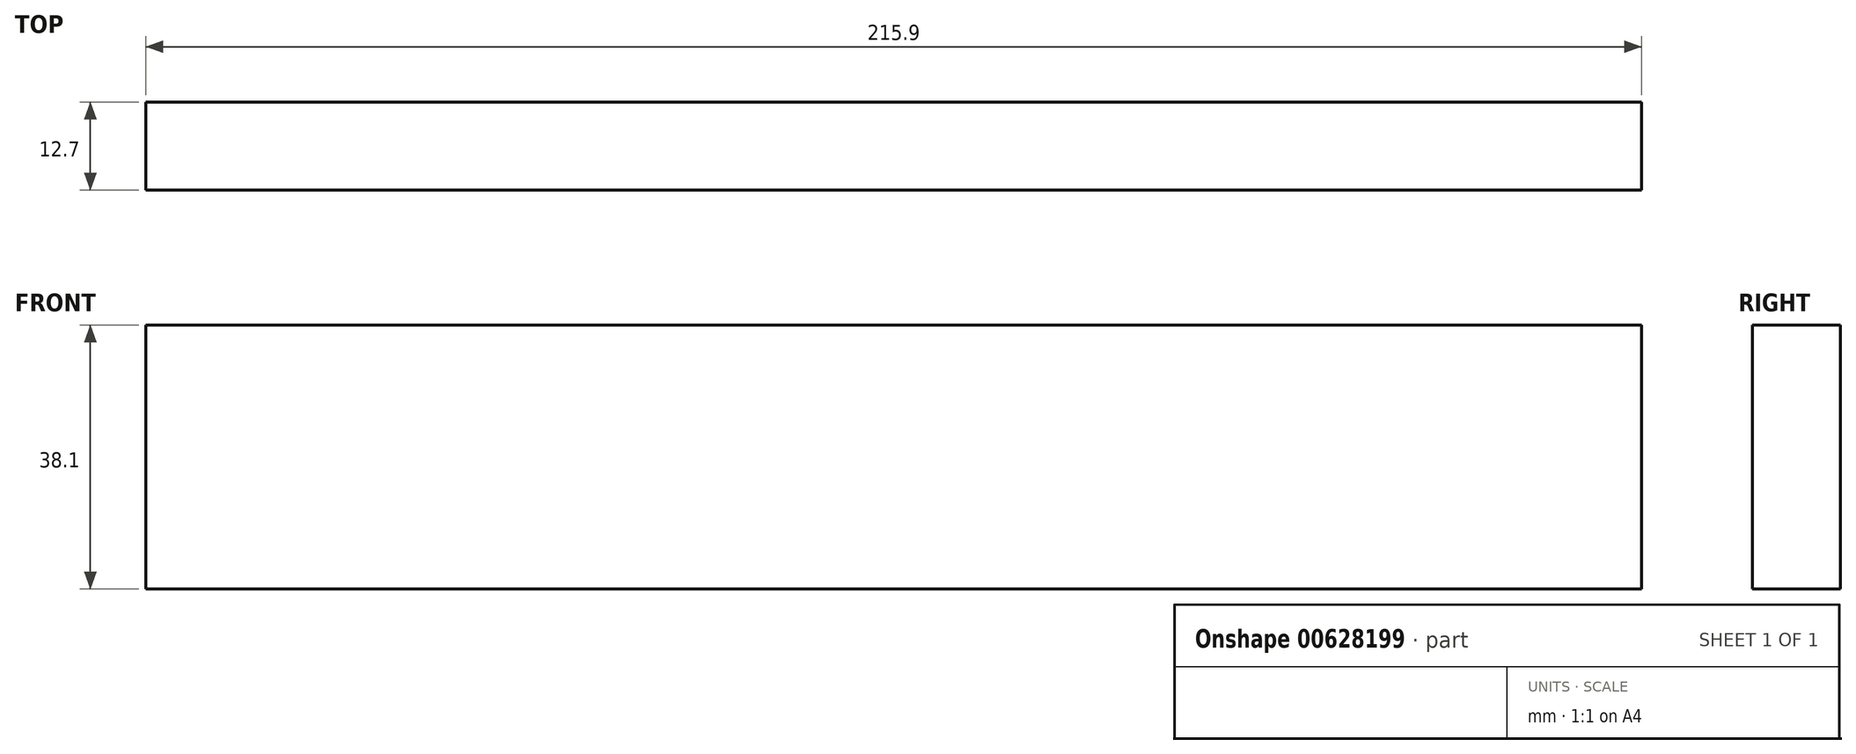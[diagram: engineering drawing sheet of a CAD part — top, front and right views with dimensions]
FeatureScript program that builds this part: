
annotation { "Feature Type Name" : "Feature", "Feature Type Description" : "" }
export const myFeature = defineFeature(function(context is Context, id is Id, definition is map)
    precondition{}
    {
        {
            var Q0;
            Q0=qCreatedBy(makeId("Front.planeOp"),FACE);
            var sketch = newSketch(context, id + "F0", { "sketchPlane" : qUnion([Q0])});
            skLineSegment(sketch, "E0.bottom", {"start": v(0, 0) * mm, "end": v(215.9, 0) * mm});
            skLineSegment(sketch, "E0.top", {"start": v(0, 38.1) * mm, "end": v(215.9, 38.1) * mm});
            skLineSegment(sketch, "E0.left", {"start": v(0, 0) * mm, "end": v(0, 38.1) * mm});
            skLineSegment(sketch, "E0.right", {"start": v(215.9, 0) * mm, "end": v(215.9, 38.1) * mm});
            skSolve(sketch);
        }
        {
            var Q0;
            Q0=qSketchRegion(id+"F0",true);
            extrude(context, id + "F1", {"entities" : qUnion([Q0]), "depth" : 12.7 * mm, "offsetDistance" : 25.4 * mm});
        }
    });
